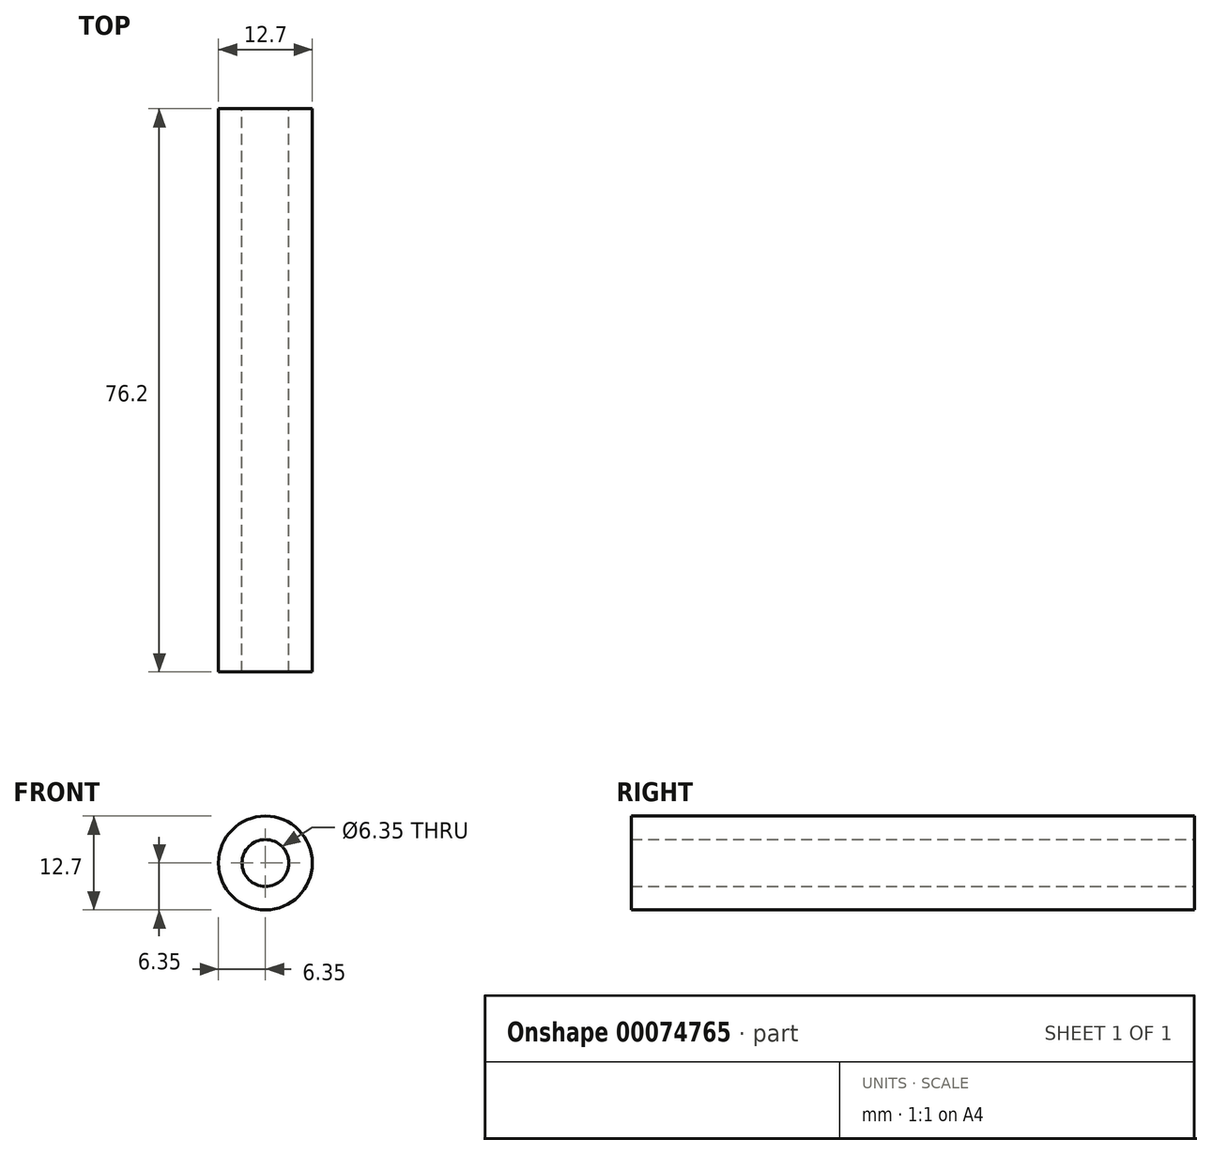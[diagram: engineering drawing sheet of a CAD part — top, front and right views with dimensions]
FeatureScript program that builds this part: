
annotation { "Feature Type Name" : "Feature", "Feature Type Description" : "" }
export const myFeature = defineFeature(function(context is Context, id is Id, definition is map)
    precondition{}
    {
        {
            var Q0;
            Q0=qCreatedBy(makeId("Front.planeOp"),FACE);
            var sketch = newSketch(context, id + "F0", { "sketchPlane" : qUnion([Q0])});
            skCircle(sketch, "E0", {"center": v(0, 0) * mm, "radius": 6.35 * mm});
            skSolve(sketch);
        }
        {
            var Q0;
            Q0=makeQuery(id+"F0.imprint","IMPRINT",FACE,{"disambiguationData":[TD([[makeQuery(id+"F0.imprint","IMPRINT",EDGE,{"derivedFrom":sQuery(id+"F0.wireOp",EDGE,"E0")}),1.0]])]});
            extrude(context, id + "F1", {"entities" : qUnion([Q0]), "oppositeDirection" : true, "depth" : 76.2 * mm});
        }
        {
            var Q0;
            Q0=qCreatedBy(makeId("Front.planeOp"),FACE);
            var sketch = newSketch(context, id + "F2", { "sketchPlane" : qUnion([Q0])});
            skPoint(sketch, "E1", {"position": v(0, 0) * mm});
            skSolve(sketch);
        }
        {
            var Q0;
            Q0=sQuery(id+"F2.wireOp",VERTEX,"E1");
            var Q1;
            Q1=makeQuery(id+"F1.opExtrude","SWEPT_BODY",BODY,{"disambiguationData":[OSD([sQuery(id+"F0.wireOp",EDGE,"E0")])]});
            hole(context, id + "F3", {"style" : HoleStyle.SIMPLE, "holeDiameter" : 6.35 * mm, "endStyle" : HoleEndStyle.THROUGH, "locations" : qUnion([Q0]), "scope" : qUnion([Q1])});
        }
    });
